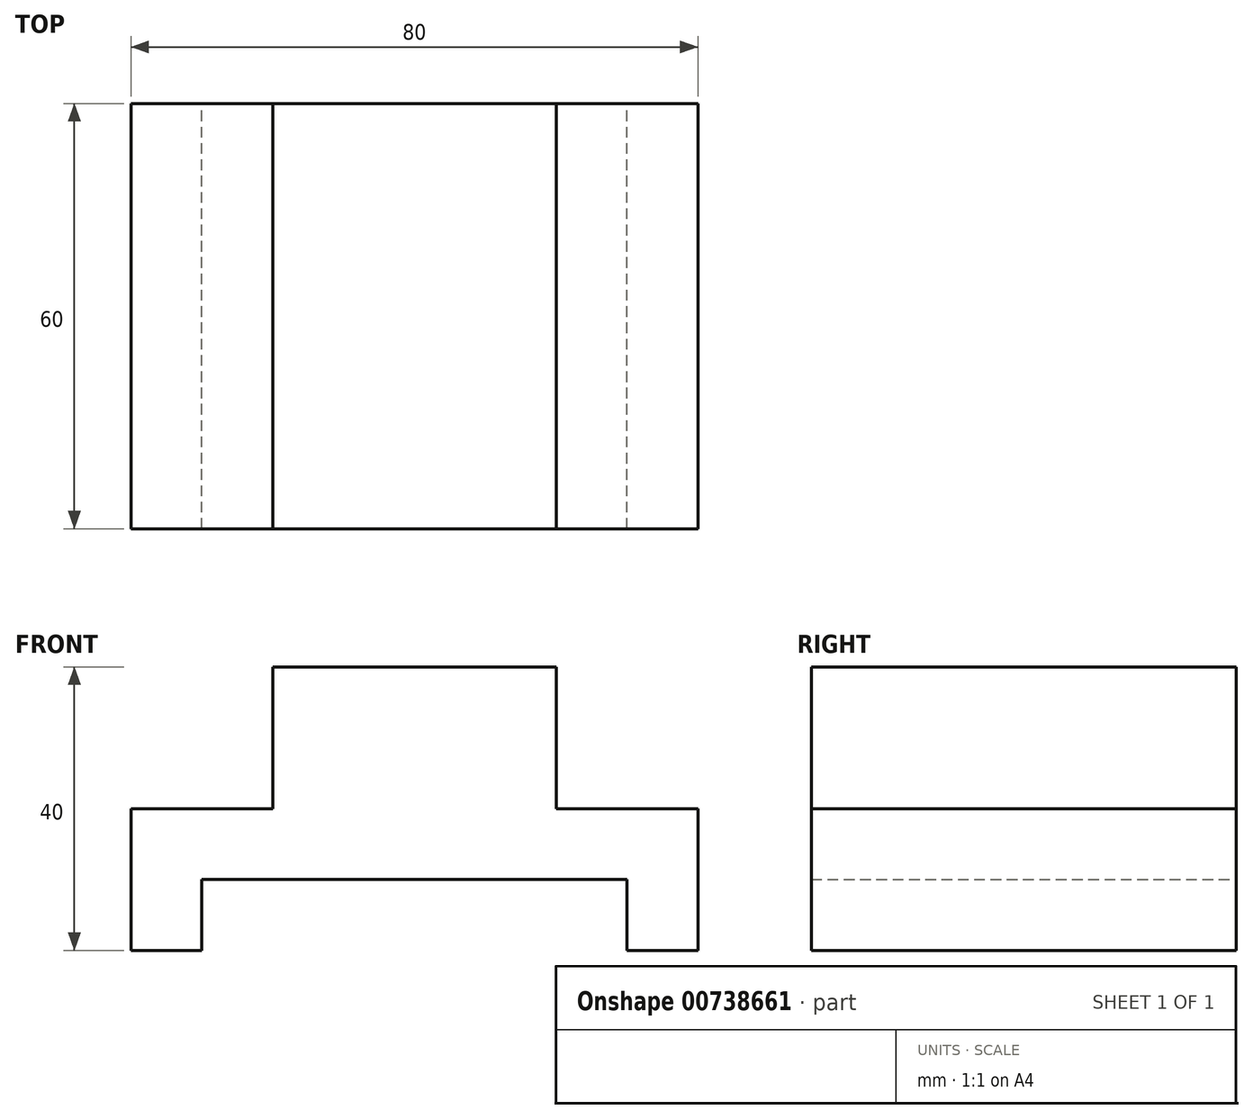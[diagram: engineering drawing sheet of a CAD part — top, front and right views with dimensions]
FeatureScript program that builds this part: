
annotation { "Feature Type Name" : "Feature", "Feature Type Description" : "" }
export const myFeature = defineFeature(function(context is Context, id is Id, definition is map)
    precondition{}
    {
        {
            var Q0;
            Q0=qCreatedBy(makeId("Front.planeOp"),FACE);
            var sketch = newSketch(context, id + "F0", { "sketchPlane" : qUnion([Q0])});
            skLineSegment(sketch, "E0", {"start": v(0, 0) * mm, "end": v(0, 20) * mm});
            skLineSegment(sketch, "E1", {"start": v(0, 20) * mm, "end": v(20, 20) * mm});
            skLineSegment(sketch, "E2", {"start": v(20, 20) * mm, "end": v(20, 40) * mm});
            skLineSegment(sketch, "E3", {"start": v(20, 40) * mm, "end": v(60, 40) * mm});
            skLineSegment(sketch, "E4", {"start": v(60, 40) * mm, "end": v(60, 20) * mm});
            skLineSegment(sketch, "E5", {"start": v(60, 20) * mm, "end": v(80, 20) * mm});
            skLineSegment(sketch, "E6", {"start": v(80, 20) * mm, "end": v(80, 0) * mm});
            skLineSegment(sketch, "E7", {"start": v(80, 0) * mm, "end": v(70, 0) * mm});
            skLineSegment(sketch, "E8", {"start": v(70, 0) * mm, "end": v(70, 10) * mm});
            skLineSegment(sketch, "E9", {"start": v(70, 10) * mm, "end": v(10, 10) * mm});
            skLineSegment(sketch, "E10", {"start": v(10, 10) * mm, "end": v(10, 0) * mm});
            skLineSegment(sketch, "E11", {"start": v(10, 0) * mm, "end": v(0, 0) * mm});
            skSolve(sketch);
        }
        {
            var Q0;
            Q0=makeQuery(id+"F0.imprint","IMPRINT",FACE,{"disambiguationData":[TD([[makeQuery(id+"F0.imprint","IMPRINT",EDGE,{"derivedFrom":sQuery(id+"F0.wireOp",EDGE,"E0")}),-1.0]])]});
            extrude(context, id + "F1", {"entities" : qUnion([Q0]), "depth" : 60 * mm, "offsetDistance" : 25 * mm});
        }
    });
